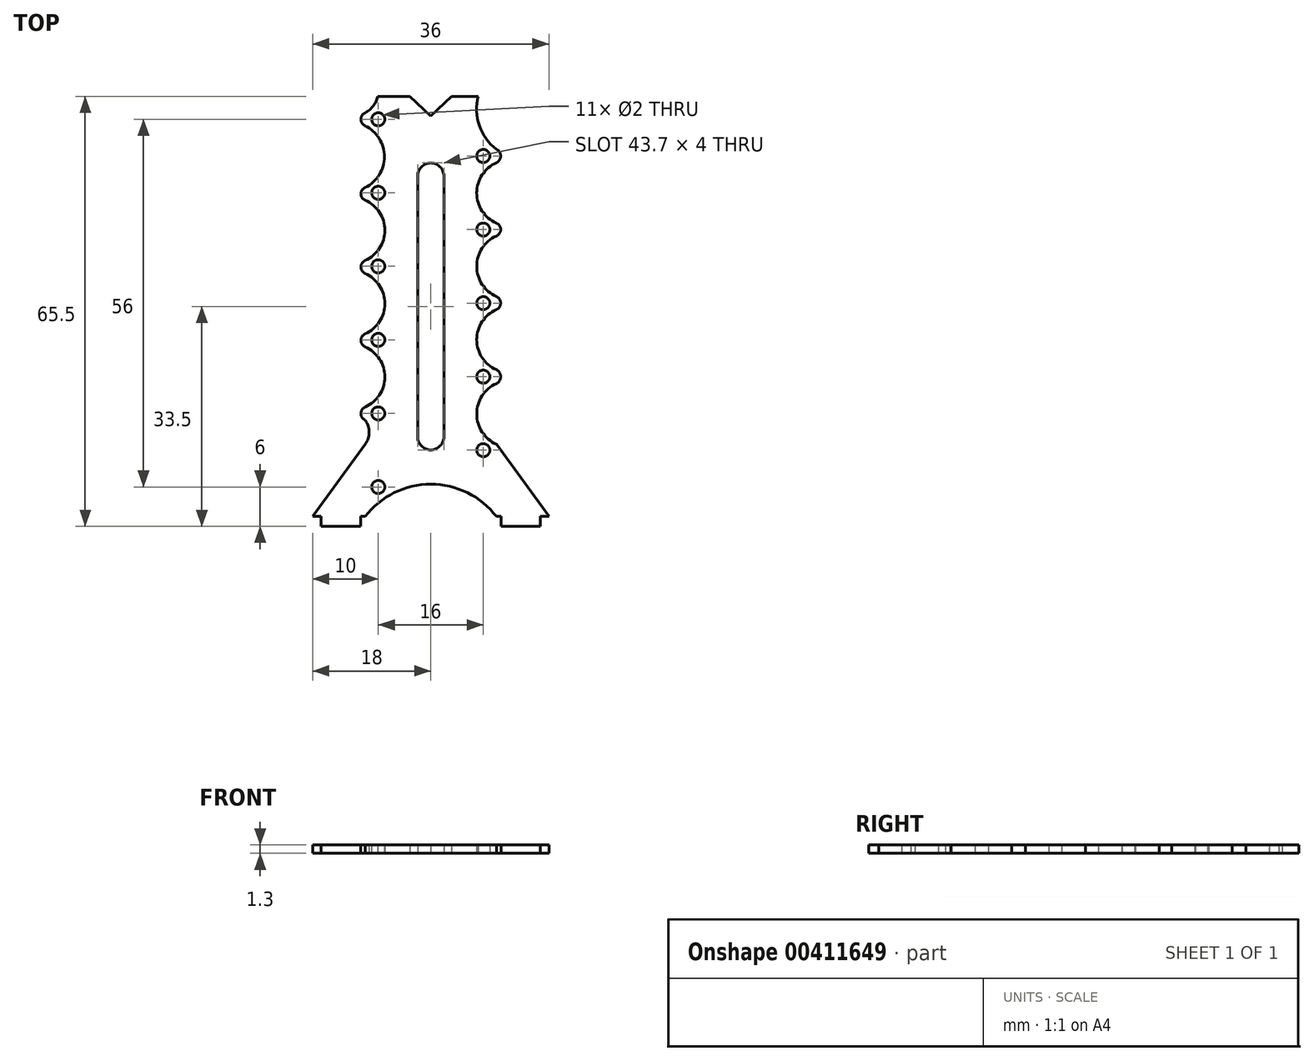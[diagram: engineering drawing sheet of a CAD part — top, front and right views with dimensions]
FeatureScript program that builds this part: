
annotation { "Feature Type Name" : "Feature", "Feature Type Description" : "" }
export const myFeature = defineFeature(function(context is Context, id is Id, definition is map)
    precondition{}
    {
        {
            var Q0;
            Q0=qCreatedBy(makeId("Top.planeOp"),FACE);
            var sketch = newSketch(context, id + "F0", { "sketchPlane" : qUnion([Q0])});
            skLineSegment(sketch, "E0.bottom", {"start": v(-18, -32) * mm, "end": v(-16.7, -32) * mm});
            skLineSegment(sketch, "E0.top", {"start": v(-8.06, 32) * mm, "end": v(-3.17, 32) * mm});
            skPoint(sketch, "E0.middle", {"position": v(0, 0) * mm});
            skLineSegment(sketch, "E1", {"start": v(18, -32) * mm, "end": v(10, -21) * mm});
            skLineSegment(sketch, "E2", {"start": v(-18, -32) * mm, "end": v(-10, -21) * mm});
            skPoint(sketch, "E3.orphan", {"position": v(18, 32) * mm});
            skPoint(sketch, "E4.orphan", {"position": v(-18, 32) * mm});
            skLineSegment(sketch, "E5", {"start": v(0, 28.99) * mm, "end": v(0, -39.22) * mm, "construction": true});
            skPoint(sketch, "E5.endSnap0", {"position": v(0, -32) * mm});
            skLineSegment(sketch, "E6", {"start": v(-8, 35.96) * mm, "end": v(-8, -17.3) * mm, "construction": true});
            skCircle(sketch, "E7", {"center": v(-8, -27.5) * mm, "radius": 1 * mm});
            skCircle(sketch, "E8", {"center": v(-8, -16.3) * mm, "radius": 1 * mm});
            skCircle(sketch, "E9", {"center": v(-8, -5.1) * mm, "radius": 1 * mm});
            skCircle(sketch, "E10", {"center": v(-8, 6.1) * mm, "radius": 1 * mm});
            skCircle(sketch, "E11", {"center": v(-8, 17.3) * mm, "radius": 1 * mm});
            skCircle(sketch, "E12", {"center": v(-8, 28.5) * mm, "radius": 1 * mm});
            skLineSegment(sketch, "E13", {"start": v(-8, -16.3) * mm, "end": v(-8, -21.9) * mm});
            skLineSegment(sketch, "E14.MirrorCS", {"start": v(8, 35.96) * mm, "end": v(8, -36.25) * mm, "construction": true});
            skCircle(sketch, "E15", {"center": v(8, -21.9) * mm, "radius": 1 * mm});
            skCircle(sketch, "E16", {"center": v(8, -10.7) * mm, "radius": 1 * mm});
            skCircle(sketch, "E17", {"center": v(8, 0.5) * mm, "radius": 1 * mm});
            skCircle(sketch, "E18", {"center": v(8, 11.7) * mm, "radius": 1 * mm});
            skCircle(sketch, "E19", {"center": v(8, 22.9) * mm, "radius": 1 * mm});
            skLineSegment(sketch, "E20.trimOffspring", {"start": v(-8, -21.9) * mm, "end": v(-8, -36.25) * mm, "construction": true});
            skArc(sketch, "E21", {"start": v(-10, 7) * mm, "mid": v(-7, 11.58) * mm, "end": v(-10, 16.17) * mm});
            skArc(sketch, "E22", {"start": v(-10, 7) * mm, "mid": v(-10.65, 6) * mm, "end": v(-10, 5) * mm});
            skArc(sketch, "E23", {"start": v(-10, -4.17) * mm, "mid": v(-7, 0.42) * mm, "end": v(-10, 5) * mm});
            skArc(sketch, "E24", {"start": v(-10, -4.17) * mm, "mid": v(-10.65, -5.16) * mm, "end": v(-10, -6.16) * mm});
            skArc(sketch, "E25", {"start": v(-10, -15.33) * mm, "mid": v(-7, -10.74) * mm, "end": v(-10, -6.16) * mm});
            skArc(sketch, "E26", {"start": v(-10, -15.33) * mm, "mid": v(-10.65, -16.33) * mm, "end": v(-9.99, -17.32) * mm});
            skArc(sketch, "E27", {"start": v(-10, -21) * mm, "mid": v(-9.4, -19.16) * mm, "end": v(-9.99, -17.32) * mm});
            skArc(sketch, "E28", {"start": v(-10, 18.11) * mm, "mid": v(-10.65, 17.14) * mm, "end": v(-10, 16.17) * mm});
            skLineSegment(sketch, "E29", {"start": v(-7, -33.31) * mm, "end": v(-7, 35.96) * mm, "construction": true});
            skPoint(sketch, "E29.startSnap0", {"position": v(-7, 0.42) * mm});
            skLineSegment(sketch, "E30", {"start": v(-10.65, -19.16) * mm, "end": v(-10.65, 41.53) * mm, "construction": true});
            skPoint(sketch, "E30.startSnap0", {"position": v(-10.65, -5.16) * mm});
            skPoint(sketch, "E30.startSnap1", {"position": v(-9.4, -19.16) * mm});
            skLineSegment(sketch, "E31.MirrorCS", {"start": v(7, -33.31) * mm, "end": v(7, 35.96) * mm, "construction": true});
            skLineSegment(sketch, "E32.MirrorCS", {"start": v(10.65, -19.16) * mm, "end": v(10.65, 41.53) * mm, "construction": true});
            skArc(sketch, "E33", {"start": v(10, -11.75) * mm, "mid": v(7, -16.38) * mm, "end": v(10, -21) * mm});
            skArc(sketch, "E34", {"start": v(10, -11.75) * mm, "mid": v(10.65, -10.7) * mm, "end": v(10, -9.65) * mm});
            skArc(sketch, "E35", {"start": v(10, -0.5) * mm, "mid": v(7, -5.07) * mm, "end": v(10, -9.65) * mm});
            skArc(sketch, "E36", {"start": v(10, -0.5) * mm, "mid": v(10.64, 0.5) * mm, "end": v(10, 1.5) * mm});
            skArc(sketch, "E37", {"start": v(10, 10.73) * mm, "mid": v(7, 6.11) * mm, "end": v(10, 1.5) * mm});
            skArc(sketch, "E38", {"start": v(10, 10.73) * mm, "mid": v(10.65, 11.7) * mm, "end": v(10, 12.68) * mm});
            skArc(sketch, "E39", {"start": v(10, 21.87) * mm, "mid": v(7, 17.28) * mm, "end": v(10, 12.68) * mm});
            skArc(sketch, "E40", {"start": v(10, 21.87) * mm, "mid": v(10.65, 22.9) * mm, "end": v(10, 23.93) * mm});
            skArc(sketch, "E41", {"start": v(7.25, 32) * mm, "mid": v(7.4, 27.55) * mm, "end": v(10, 23.93) * mm});
            skPoint(sketch, "E42.orphan", {"position": v(-10, 35.2) * mm});
            skPoint(sketch, "E43.orphan", {"position": v(-10, 32) * mm});
            skPoint(sketch, "E44.orphan", {"position": v(10, 36.12) * mm});
            skPoint(sketch, "E45.trimOffspring.end.orphan", {"position": v(10, 32) * mm});
            skArc(sketch, "E46", {"start": v(-10, 18.11) * mm, "mid": v(-7.06, 22.8) * mm, "end": v(-10, 27.5) * mm});
            skArc(sketch, "E47", {"start": v(-10, 29.5) * mm, "mid": v(-10.65, 28.5) * mm, "end": v(-10, 27.5) * mm});
            skArc(sketch, "E48", {"start": v(-10, 29.5) * mm, "mid": v(-8.75, 30.53) * mm, "end": v(-8.06, 32) * mm});
            skPoint(sketch, "E49.orphan", {"position": v(-10, 36.13) * mm});
            skLineSegment(sketch, "E50", {"start": v(-3.17, 32) * mm, "end": v(0, 28.99) * mm});
            skLineSegment(sketch, "E51.MirrorCS", {"start": v(3.17, 32) * mm, "end": v(0, 28.99) * mm});
            skPoint(sketch, "E52.orphan", {"position": v(0, 35.6) * mm});
            skLineSegment(sketch, "E53.trimOffspring", {"start": v(3.17, 32) * mm, "end": v(7.25, 32) * mm});
            skLineSegment(sketch, "E54.trimOffspring", {"start": v(3.17, 32) * mm, "end": v(8, 32) * mm});
            skLineSegment(sketch, "E55", {"start": v(-16.7, -33.5) * mm, "end": v(-10.7, -33.5) * mm});
            skLineSegment(sketch, "E56", {"start": v(16.7, -32) * mm, "end": v(16.7, -33.5) * mm});
            skLineSegment(sketch, "E57", {"start": v(10.7, -32) * mm, "end": v(10.7, -33.5) * mm});
            skLineSegment(sketch, "E58.MirrorCS", {"start": v(-10.7, -32) * mm, "end": v(-10.7, -33.5) * mm});
            skLineSegment(sketch, "E59.MirrorCS", {"start": v(-16.7, -32) * mm, "end": v(-16.7, -33.5) * mm});
            skLineSegment(sketch, "E60.trimOffspring", {"start": v(16.7, -32) * mm, "end": v(18, -32) * mm});
            skPoint(sketch, "E61.trimOffspring.end.orphan", {"position": v(19.92, -33.5) * mm});
            skPoint(sketch, "E61.trimOffspring.start.orphan", {"position": v(18.2, -33.5) * mm});
            skPoint(sketch, "E62.orphan", {"position": v(-18.2, -33.5) * mm});
            skLineSegment(sketch, "E63", {"start": v(10.7, -33.5) * mm, "end": v(16.7, -33.5) * mm});
            skLineSegment(sketch, "E64.bottom", {"start": v(0, -21.85) * mm, "end": v(0, -21.85) * mm});
            skLineSegment(sketch, "E64.top", {"start": v(0, 21.85) * mm, "end": v(0, 21.85) * mm});
            skLineSegment(sketch, "E64.left", {"start": v(-2, -19.85) * mm, "end": v(-2, 19.85) * mm});
            skLineSegment(sketch, "E64.right", {"start": v(2, -19.85) * mm, "end": v(2, 19.85) * mm});
            skPoint(sketch, "E65.visualSharp", {"position": v(-2, 21.85) * mm});
            skArc(sketch, "E65.filletArc", {"start": v(0, 21.85) * mm, "mid": v(-1.41, 21.27) * mm, "end": v(-2, 19.85) * mm});
            skPoint(sketch, "E66.visualSharp", {"position": v(2, 21.85) * mm});
            skArc(sketch, "E66.filletArc", {"start": v(2, 19.85) * mm, "mid": v(1.41, 21.27) * mm, "end": v(0, 21.85) * mm});
            skPoint(sketch, "E67.visualSharp", {"position": v(-2, -21.85) * mm});
            skArc(sketch, "E67.filletArc", {"start": v(-2, -19.85) * mm, "mid": v(-1.41, -21.27) * mm, "end": v(0, -21.85) * mm});
            skPoint(sketch, "E68.visualSharp", {"position": v(2, -21.85) * mm});
            skArc(sketch, "E68.filletArc", {"start": v(0, -21.85) * mm, "mid": v(1.41, -21.27) * mm, "end": v(2, -19.85) * mm});
            skArc(sketch, "E69", {"start": v(10, -32) * mm, "mid": v(0, -27.08) * mm, "end": v(-10, -32) * mm});
            skLineSegment(sketch, "E70", {"start": v(10, -32) * mm, "end": v(10.7, -32) * mm});
            skLineSegment(sketch, "E71", {"start": v(-10.7, -32) * mm, "end": v(-10, -32) * mm});
            skPoint(sketch, "E72.trimOffspring.end.orphan", {"position": v(-19.92, -33.5) * mm});
            skSolve(sketch);
        }
        {
            var Q0;
            Q0=makeQuery(id+"F0.imprint","IMPRINT",FACE,{"disambiguationData":[TD([[makeQuery(id+"F0.imprint","IMPRINT",EDGE,{"derivedFrom":sQuery(id+"F0.wireOp",EDGE,"E0.bottom")}),1.0]])]});
            extrude(context, id + "F1", {"entities" : qUnion([Q0]), "depth" : 1.3 * mm});
        }
    });
